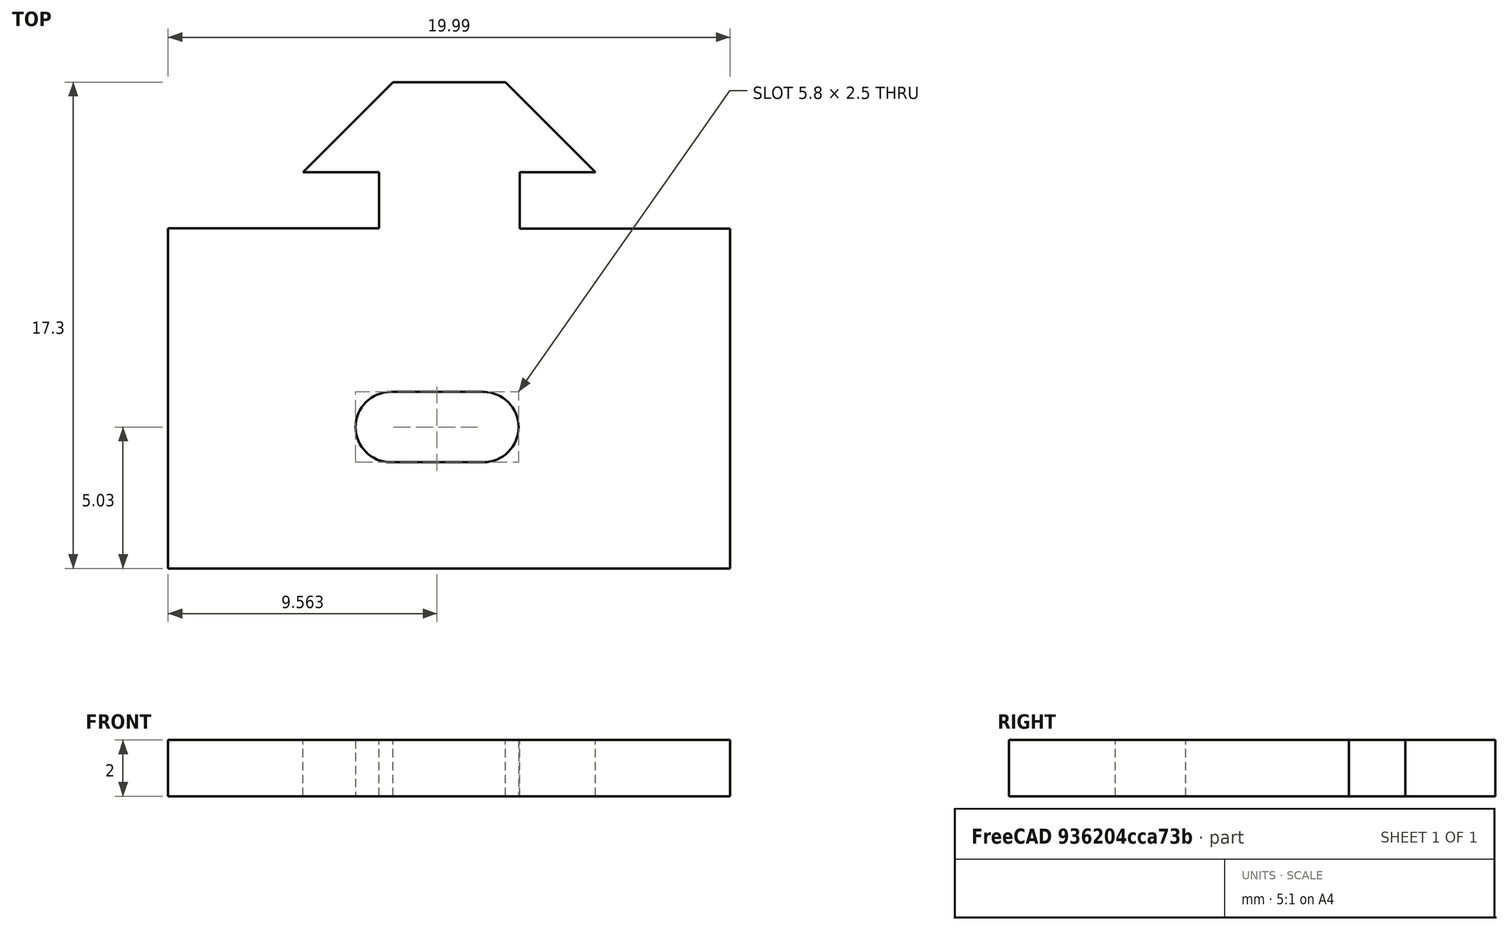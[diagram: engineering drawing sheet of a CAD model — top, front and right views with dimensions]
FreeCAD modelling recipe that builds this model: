
FCSTD DOCUMENT  (FreeCAD 0.18R4 (GitTag))
Label: support-y-back
License: All rights reserved
LicenseURL: http://en.wikipedia.org/wiki/All_rights_reserved
objects: Sketcher::SketchObject×2, PartDesign::Pad×1, PartDesign::Pocket×1, PartDesign::Body×1
note: 7 computed .brp shape members not serialized (recipe doc carries the construction recipe); baked Part::Feature solids carry a one-line shape summary decoded from their .brp

FEATURE [Sketcher::SketchObject] Sketch003
  MapMode = 5
  Placement = pos=(0,0,100) rot=(0,0,1;0rad)
  sketch-geometry (34):
    g0: LineSegment StartX=19.9888 StartY=-0.010854 StartZ=0 EndX=12.5 EndY=-0.010854 EndZ=0
    g1: LineSegment [constr] StartX=13 StartY=-0.5 StartZ=0 EndX=13 EndY=1.5 EndZ=0
    g2: LineSegment [constr] StartX=13 StartY=1.5 StartZ=0 EndX=16 EndY=1.5 EndZ=0
    g3: LineSegment [constr] StartX=16 StartY=1.5 StartZ=0 EndX=12 EndY=5.5 EndZ=0
    g4: LineSegment [constr] StartX=12 StartY=5.5 StartZ=0 EndX=8 EndY=5.5 EndZ=0
    g5: LineSegment [constr] StartX=8 StartY=5.5 StartZ=0 EndX=4 EndY=1.5 EndZ=0
    g6: LineSegment [constr] StartX=4 StartY=1.5 StartZ=0 EndX=7 EndY=1.5 EndZ=0
    g7: LineSegment [constr] StartX=7 StartY=1.5 StartZ=0 EndX=7 EndY=-0.5 EndZ=0
    g8: LineSegment StartX=7.5 StartY=0 StartZ=0 EndX=0 EndY=0 EndZ=0
    g9: LineSegment [constr] StartX=95 StartY=13.1875 StartZ=0 EndX=95 EndY=-40.4075 EndZ=0
    g10: GeomPoint X=47.5 Y=6.34377 Z=0
    g11: LineSegment [constr] StartX=47.5 StartY=30.795 StartZ=0 EndX=47.5 EndY=-44.5049 EndZ=0
    g12: LineSegment [constr] StartX=95 StartY=-0.5 StartZ=0 EndX=95 EndY=-20.0529 EndZ=0
    g13: LineSegment [constr] StartX=95 StartY=-20.0529 StartZ=0 EndX=0 EndY=-20.0529 EndZ=0
    g14: LineSegment [constr] StartX=75 StartY=-0.5 StartZ=0 EndX=82 EndY=-0.5 EndZ=0
    g15: LineSegment [constr] StartX=82 StartY=-0.5 StartZ=0 EndX=82 EndY=1.5 EndZ=0
    g16: LineSegment [constr] StartX=82 StartY=1.5 StartZ=0 EndX=79 EndY=1.5 EndZ=0
    g17: LineSegment [constr] StartX=79 StartY=1.5 StartZ=0 EndX=83 EndY=5.5 EndZ=0
    g18: LineSegment [constr] StartX=83 StartY=5.5 StartZ=0 EndX=87 EndY=5.5 EndZ=0
    g19: LineSegment [constr] StartX=87 StartY=5.5 StartZ=0 EndX=91 EndY=1.5 EndZ=0
    g20: LineSegment [constr] StartX=91 StartY=1.5 StartZ=0 EndX=88 EndY=1.5 EndZ=0
    g21: LineSegment [constr] StartX=88 StartY=1.5 StartZ=0 EndX=88 EndY=-0.5 EndZ=0
    g22: LineSegment [constr] StartX=88 StartY=-0.5 StartZ=0 EndX=95 EndY=-0.5 EndZ=0
    g23: LineSegment [constr] StartX=20 StartY=-0.5 StartZ=0 EndX=75 EndY=-0.5 EndZ=0
    g24: LineSegment StartX=7.5 StartY=0 StartZ=0 EndX=7.5 EndY=2 EndZ=0
    g25: LineSegment StartX=7.5 StartY=2 StartZ=0 EndX=4.8 EndY=2 EndZ=0
    g26: LineSegment StartX=4.8 StartY=2 StartZ=0 EndX=8 EndY=5.2 EndZ=0
    g27: LineSegment StartX=8 StartY=5.2 StartZ=0 EndX=12 EndY=5.2 EndZ=0
    g28: LineSegment StartX=12 StartY=5.2 StartZ=0 EndX=15.2 EndY=2 EndZ=0
    g29: LineSegment StartX=15.2 StartY=2 StartZ=0 EndX=12.5 EndY=2 EndZ=0
    g30: LineSegment StartX=12.5 StartY=2 StartZ=0 EndX=12.5 EndY=-0.010854 EndZ=0
    g31: LineSegment StartX=0 StartY=0 StartZ=0 EndX=0 EndY=-12.1032 EndZ=0
    g32: LineSegment StartX=0 StartY=-12.1032 StartZ=0 EndX=19.9888 EndY=-12.1032 EndZ=0
    g33: LineSegment StartX=19.9888 StartY=-12.1032 StartZ=0 EndX=19.9888 EndY=-0.010854 EndZ=0
  constraints (46):
    c: Vertical(g9)
    c: Vertical(g11)
    c: PointOnObject(g10,g11)
    c: Vertical(g12)
    c: Block(g22)
    c: Block(g14)
    c: Block(g12)
    c: Coincident(g24,g25)
    c: Coincident(g25,g26)
    c: Coincident(g26,g27)
    c: Coincident(g27,g28)
    c: Coincident(g28,g29)
    c: Coincident(g29,g30)
    c: Vertical(g24)
    c: Vertical(g30)
    c: Horizontal(g25)
    c: Horizontal(g27)
    c: Horizontal(g29)
    c: Block(g1)
    c: Block(g2)
    c: Block(g3)
    c: Block(g4)
    c: Block(g5)
    c: Block(g6)
    c: Block(g7)
    c: DistanceX(g6,g24) = 0.5
    c: DistanceX(g4,g26) = 0
    c: DistanceX(g29,g1) = 0.5
    c: DistanceY(g6,g24) = 0.5
    c: DistanceY(g26,g4) = 0.3
    c: DistanceY(g1,g29) = 0.5
    c: Parallel(g5,g26)
    c: Parallel(g3,g28)
    c: DistanceX(g27,g3) = 0
    c: Horizontal(g8)
    c: Coincident(g31,g32)
    c: Coincident(g32,g33)
    c: Coincident(g33,g0)
    c: Coincident(g31,g8)
    c: Coincident(g8,g24)
    c: Coincident(g0,g30)
    c: Horizontal(g0)
    c: Coincident(g8,g-1)
    c: Vertical(g31)
    c: Vertical(g33)
    c: Horizontal(g32)
FEATURE [PartDesign::Pad] Pad
  Length = 2
  Length2 = 100
  Placement = pos=(0,0,100) rot=(0,0,1;0rad)
  Profile = -> Sketch003
  Type = 0
FEATURE [Sketcher::SketchObject] Sketch
  MapMode = 5
  Placement = pos=(0,0,100) rot=(1,0,0;3.14159rad)
  Support = -> [Pad]
  sketch-geometry (4):
    g0: ArcOfCircle CenterX=7.91752 CenterY=7.07034 CenterZ=0 NormalX=0 NormalY=0 NormalZ=1 AngleXU=0 Radius=1.25204 StartAngle=1.5708 EndAngle=4.71239
    g1: ArcOfCircle CenterX=11.2086 CenterY=7.07034 CenterZ=0 NormalX=0 NormalY=0 NormalZ=1 AngleXU=0 Radius=1.25204 StartAngle=4.71239 EndAngle=7.85398
    g2: LineSegment StartX=7.91752 StartY=5.81829 StartZ=0 EndX=11.2086 EndY=5.81829 EndZ=0
    g3: LineSegment StartX=7.91752 StartY=8.32238 StartZ=0 EndX=11.2086 EndY=8.32238 EndZ=0
  constraints (6):
    c: Tangent(g0,g3) = 1.5708
    c: Tangent(g0,g2) = -1.5708
    c: Tangent(g2,g1) = -1.5708
    c: Tangent(g3,g1) = 1.5708
    c: Horizontal(g2)
    c: Equal(g0,g1)
FEATURE [PartDesign::Pocket] Pocket
  BaseFeature = -> Pad
  Length = 5
  Length2 = 100
  Placement = pos=(0,0,100) rot=(0,0,1;0rad)
  Profile = -> Sketch
  Type = 0
FEATURE [PartDesign::Body] Body
  Group = -> [Sketch003,Pad,Sketch,Pocket]
  Origin = -> Origin
  Tip = -> Pocket
